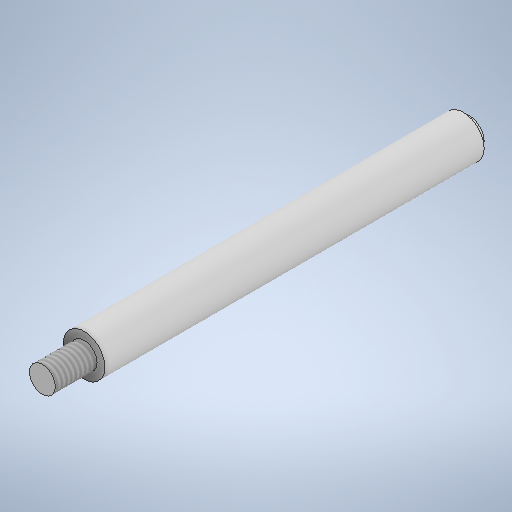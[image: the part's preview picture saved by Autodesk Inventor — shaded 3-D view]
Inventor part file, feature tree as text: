
AUTODESK INVENTOR PART (.ipt)
format: ipt  version: 2025.1 (Build 291241000, 241)  size: 256,512 bytes
history: native  units: mm
features: revolve x1, thread x1, chamfer x1, sketch x1
ambient origin geometry x8: Origin, YZ Plane, XZ Plane, XY Plane, X Axis, Y Axis, Z Axis, Center Point
bodies: Solid1 (feature_tree)
feature tree (4):
  revolve  "Revolution1"  [1 undecoded]
  thread  "Thread1"  [1 undecoded]
  chamfer  "Chamfer1"  Distance=2.5mm
  sketch  "Sketch1"  dims[d0=41.0mm d1=4.0mm d2=4.0mm d3=2.5mm d4=90.0deg d5=4.0mm d6=0.0mm d7=0.6mm d8=2.0mm d9=45.0deg]
note: 2 required parameter values undecoded (feature->parameter linkage not recoverable at this tier; creation-order binding heuristic only, values carry confidence <= 0.55)